# Revit family: 32_Berkvens_Avento RZ 201
name_source: partatom
category: Doors
units: mm (PartAtom-declared; Revit-internal decimal feet)

## family parameters
Always vertical = Yes
Cut with Voids When Loaded = No
Host = Wall
OmniClass Number = 23.30.10.00
OmniClass Title = Doors
Room Calculation Point = No
Shared = No

## types (3) — shared parameters
60_45 Model kozijn = RZ glaspui
60_81 Uitvoering kozijn = Glaspui zonder bovenlicht
60_84 Type kozijn = Avento stalen montagekozijn 1,5 mm
80_60 Kantuitvoering = stomp
80_75 Deurhoogte = 2315 mm  [stored 7.59514 ft]
Analytic Construction = <None>
Function = Interior
M1 = Berkvens <maak keuze>
M2 = Berkvens_kristalwit
M3 = Berkvens_reinwit
M4 = Berkvens_reinwit
M5 = Berkvens_kristalwit
M6 = Berkvens_gebroken wit
Manufacturer = Berkvens
Model = Avento RZ
URL = www.berkvens.nl
Versie = 1.0
Wall Closure = By host
zero-valued in all types: Height, Width

## per-type parameters (varying)
| type | 60_48 Totale breedte | 60_51 Sparingsmaat | 60_63 Vloerplafondhoogte | Assembly Code | Compartmentation | FireExit | IsExternal | SelfClosing | SmokeStop |
| 1000X2315 | 1000 mm  [stored 3.28084 ft] | 970 mm  [stored 3.18241 ft] | 0 mm  [stored 0 ft] | 32.31 | No | No | No | No | No |
| 880x2315 | 955 mm  [stored 3.1332 ft] | 925 mm  [stored 3.03478 ft] | 2650 mm  [stored 8.69423 ft] |  | Yes | Yes | Yes | Yes | Yes |
| 730x2315 | 955 mm  [stored 3.1332 ft] | 925 mm  [stored 3.03478 ft] | 2650 mm  [stored 8.69423 ft] |  | Yes | Yes | Yes | Yes | Yes |

note: [stored X ft] marks values corroborated as IEEE doubles in the binary element streams (Revit-internal decimal feet)

## geometry (parser evidence)
native form markers: Sweep x7
no freeform markers — native parametric forms only
